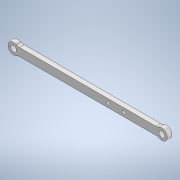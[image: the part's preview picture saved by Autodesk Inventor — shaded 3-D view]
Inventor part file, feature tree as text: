
AUTODESK INVENTOR PART (.ipt)
format: ipt  version: 2020 (Build 240168000, 168)  size: 133,120 bytes
history: native  units: mm
features: extrude x2, sketch x2, fillet x1
ambient origin geometry x8: Origin, YZ Plane, XZ Plane, XY Plane, X Axis, Y Axis, Z Axis, Center Point
bodies: Solid1 (feature_tree)
feature tree (5):
  extrude  "Extrusion1"  Depth=4.0mm
  fillet  "Fillet2"  Radius=1.5mm
  extrude  "Extrusion2"  Depth=47.0mm
  sketch  "Sketch1"  dims[d0=2.0mm d1=4.0mm d4=1.5mm d5=0.0mm]
  sketch  "Sketch3"  dims[d8=3.0mm d9=47.0mm d10=2.0mm d11=12.0mm d12=5.0mm d13=1.5mm d14=0.0mm d15=0.0mm]
